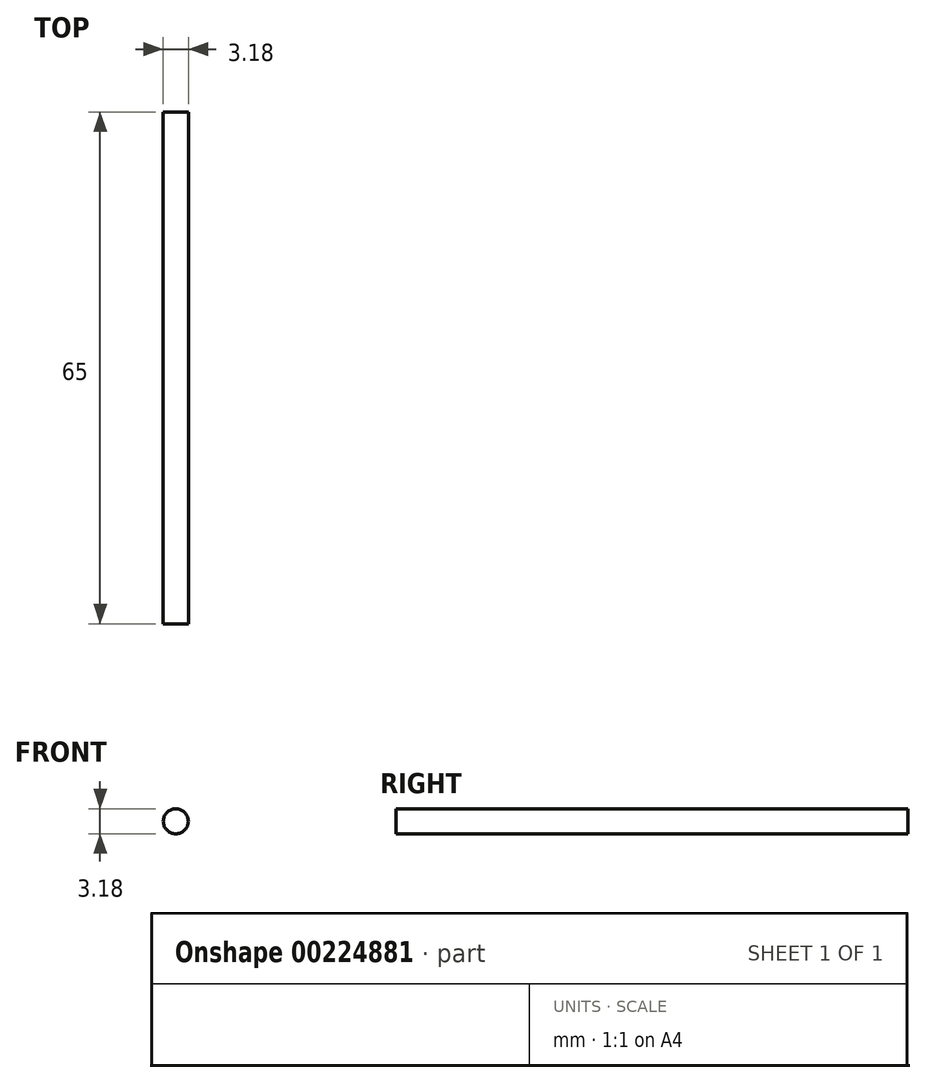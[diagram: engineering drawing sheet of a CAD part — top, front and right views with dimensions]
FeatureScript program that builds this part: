
annotation { "Feature Type Name" : "Feature", "Feature Type Description" : "" }
export const myFeature = defineFeature(function(context is Context, id is Id, definition is map)
    precondition{}
    {
        {
            var Q0;
            Q0=qCreatedBy(makeId("Front.planeOp"),FACE);
            var sketch = newSketch(context, id + "F0", { "sketchPlane" : qUnion([Q0])});
            skCircle(sketch, "E0", {"center": v(0, 0) * mm, "radius": 1.59 * mm});
            skSolve(sketch);
        }
        {
            var Q0;
            Q0 = qSketchRegion(id + "F0", true);
            extrude(context, id + "F1", {"entities" : qUnion([Q0]), "endBound" : BoundingType.SYMMETRIC, "depth" : 65 * mm});
        }
    });
